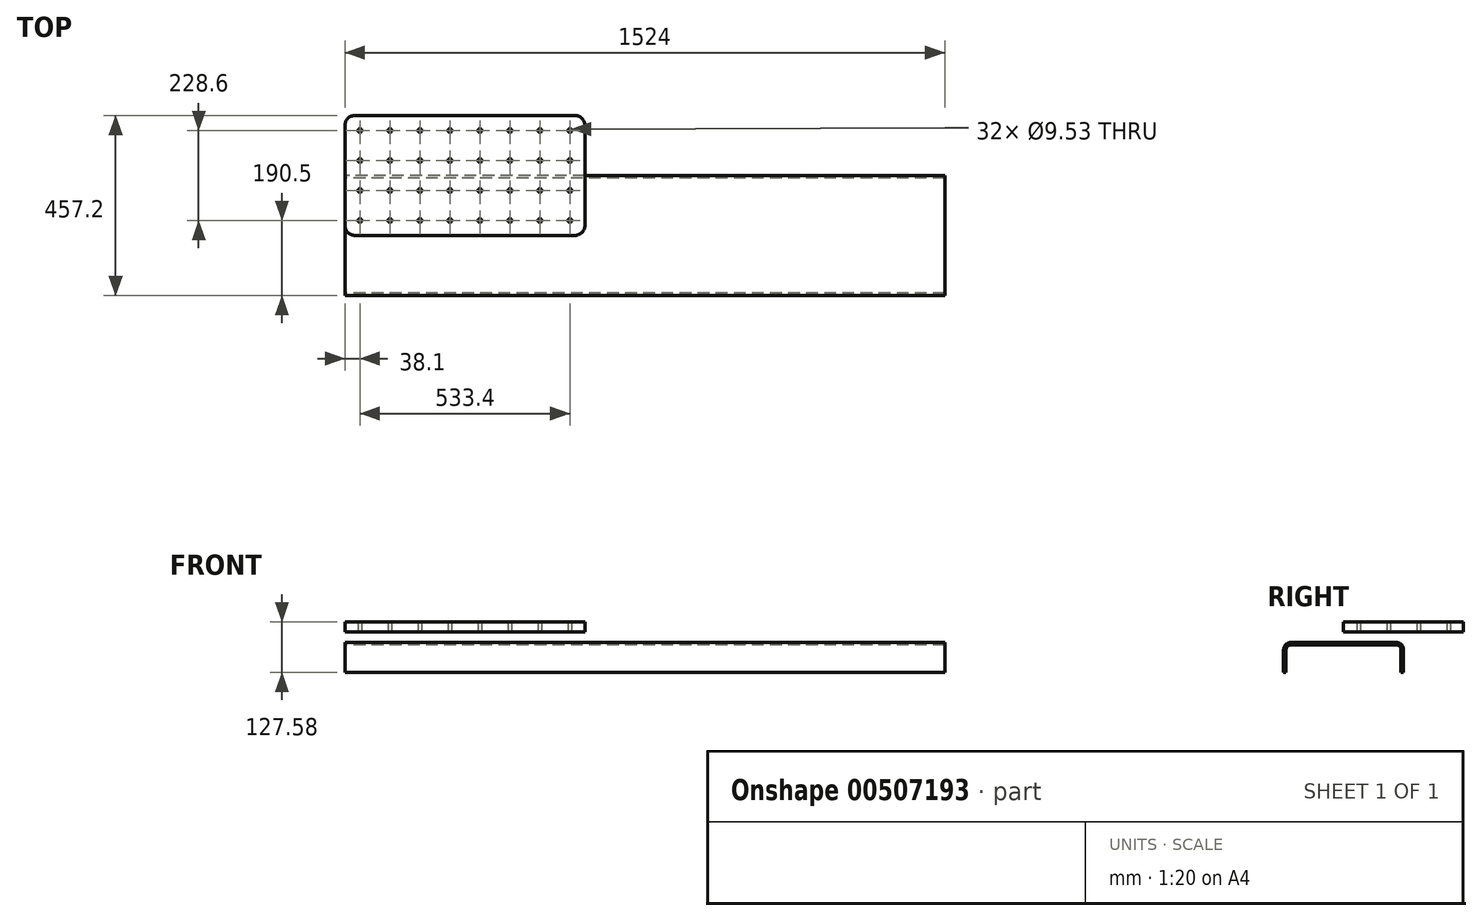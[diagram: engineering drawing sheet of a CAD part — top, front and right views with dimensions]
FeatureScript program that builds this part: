
annotation { "Feature Type Name" : "Feature", "Feature Type Description" : "" }
export const myFeature = defineFeature(function(context is Context, id is Id, definition is map)
    precondition{}
    {
        {
            var Q0;
            Q0=qCreatedBy(makeId("Top.planeOp"),FACE);
            var sketch = newSketch(context, id + "F0", { "sketchPlane" : qUnion([Q0])});
            skLineSegment(sketch, "E0", {"start": v(0, 0) * mm, "end": v(0, 304.8) * mm});
            skLineSegment(sketch, "E1", {"start": v(0, 304.8) * mm, "end": v(609.6, 304.8) * mm});
            skLineSegment(sketch, "E2", {"start": v(609.6, 304.8) * mm, "end": v(609.6, 0) * mm});
            skLineSegment(sketch, "E3", {"start": v(609.6, 0) * mm, "end": v(0, 0) * mm});
            skCircle(sketch, "E4", {"center": v(38.1, 38.1) * mm, "radius": 4.76 * mm});
            skCircle(sketch, "E5.0.1.0", {"center": v(38.1, 114.3) * mm, "radius": 4.76 * mm});
            skCircle(sketch, "E5.0.2.0", {"center": v(38.1, 190.5) * mm, "radius": 4.76 * mm});
            skCircle(sketch, "E5.0.3.0", {"center": v(38.1, 266.7) * mm, "radius": 4.76 * mm});
            skCircle(sketch, "E5.1.0.0", {"center": v(114.3, 38.1) * mm, "radius": 4.76 * mm});
            skCircle(sketch, "E5.1.1.0", {"center": v(114.3, 114.3) * mm, "radius": 4.76 * mm});
            skCircle(sketch, "E5.1.2.0", {"center": v(114.3, 190.5) * mm, "radius": 4.76 * mm});
            skCircle(sketch, "E5.1.3.0", {"center": v(114.3, 266.7) * mm, "radius": 4.76 * mm});
            skCircle(sketch, "E5.2.0.0", {"center": v(190.5, 38.1) * mm, "radius": 4.76 * mm});
            skCircle(sketch, "E5.2.1.0", {"center": v(190.5, 114.3) * mm, "radius": 4.76 * mm});
            skCircle(sketch, "E5.2.2.0", {"center": v(190.5, 190.5) * mm, "radius": 4.76 * mm});
            skCircle(sketch, "E5.2.3.0", {"center": v(190.5, 266.7) * mm, "radius": 4.76 * mm});
            skCircle(sketch, "E5.3.0.0", {"center": v(266.7, 38.1) * mm, "radius": 4.76 * mm});
            skCircle(sketch, "E5.3.1.0", {"center": v(266.7, 114.3) * mm, "radius": 4.76 * mm});
            skCircle(sketch, "E5.3.2.0", {"center": v(266.7, 190.5) * mm, "radius": 4.76 * mm});
            skCircle(sketch, "E5.3.3.0", {"center": v(266.7, 266.7) * mm, "radius": 4.76 * mm});
            skCircle(sketch, "E5.4.0.0", {"center": v(342.9, 38.1) * mm, "radius": 4.76 * mm});
            skCircle(sketch, "E5.4.1.0", {"center": v(342.9, 114.3) * mm, "radius": 4.76 * mm});
            skCircle(sketch, "E5.4.2.0", {"center": v(342.9, 190.5) * mm, "radius": 4.76 * mm});
            skCircle(sketch, "E5.4.3.0", {"center": v(342.9, 266.7) * mm, "radius": 4.76 * mm});
            skCircle(sketch, "E5.5.0.0", {"center": v(419.1, 38.1) * mm, "radius": 4.76 * mm});
            skCircle(sketch, "E5.5.1.0", {"center": v(419.1, 114.3) * mm, "radius": 4.76 * mm});
            skCircle(sketch, "E5.5.2.0", {"center": v(419.1, 190.5) * mm, "radius": 4.76 * mm});
            skCircle(sketch, "E5.5.3.0", {"center": v(419.1, 266.7) * mm, "radius": 4.76 * mm});
            skCircle(sketch, "E5.6.0.0", {"center": v(495.3, 38.1) * mm, "radius": 4.76 * mm});
            skCircle(sketch, "E5.6.1.0", {"center": v(495.3, 114.3) * mm, "radius": 4.76 * mm});
            skCircle(sketch, "E5.6.2.0", {"center": v(495.3, 190.5) * mm, "radius": 4.76 * mm});
            skCircle(sketch, "E5.6.3.0", {"center": v(495.3, 266.7) * mm, "radius": 4.76 * mm});
            skCircle(sketch, "E5.7.0.0", {"center": v(571.5, 38.1) * mm, "radius": 4.76 * mm});
            skCircle(sketch, "E5.7.1.0", {"center": v(571.5, 114.3) * mm, "radius": 4.76 * mm});
            skCircle(sketch, "E5.7.2.0", {"center": v(571.5, 190.5) * mm, "radius": 4.76 * mm});
            skCircle(sketch, "E5.7.3.0", {"center": v(571.5, 266.7) * mm, "radius": 4.76 * mm});
            skLineSegment(sketch, "E5.direction1", {"start": v(38.1, 38.1) * mm, "end": v(114.3, 38.1) * mm, "construction": true});
            skLineSegment(sketch, "E5.direction2", {"start": v(38.1, 38.1) * mm, "end": v(38.1, 114.3) * mm, "construction": true});
            skSolve(sketch);
        }
        {
            var Q0;
            Q0 = qSketchRegion(id + "F0", true);
            extrude(context, id + "F1", {"entities" : qUnion([Q0]), "depth" : 25.4 * mm});
        }
        {
            var Q0;
            Q0=makeQuery(id+"F1.opExtrude","SWEPT_EDGE",EDGE,{"disambiguationData":[OSD([sQuery(id+"F0.wireOp",EDGE,"E0"),sQuery(id+"F0.wireOp",EDGE,"E3")])]});
            var Q1;
            Q1=makeQuery(id+"F1.opExtrude","SWEPT_EDGE",EDGE,{"disambiguationData":[OSD([sQuery(id+"F0.wireOp",EDGE,"E2"),sQuery(id+"F0.wireOp",EDGE,"E3")])]});
            var Q2;
            Q2=makeQuery(id+"F1.opExtrude","SWEPT_EDGE",EDGE,{"disambiguationData":[OSD([sQuery(id+"F0.wireOp",EDGE,"E1"),sQuery(id+"F0.wireOp",EDGE,"E2")])]});
            var Q3;
            Q3=makeQuery(id+"F1.opExtrude","SWEPT_EDGE",EDGE,{"disambiguationData":[OSD([sQuery(id+"F0.wireOp",EDGE,"E0"),sQuery(id+"F0.wireOp",EDGE,"E1")])]});
            fillet(context, id + "F2", {"entities" : qUnion([Q0, Q1, Q2, Q3]), "radius" : 25.4 * mm, "tangentPropagation" : true, "allowEdgeOverflow" : false});
        }
        {
            var Q0;
            Q0=qCreatedBy(makeId("Right.planeOp"),FACE);
            var sketch = newSketch(context, id + "F3", { "sketchPlane" : qUnion([Q0])});
            skLineSegment(sketch, "E6", {"start": v(0, -25.98) * mm, "end": v(-133.35, -25.98) * mm});
            skArc(sketch, "E7", {"start": v(-133.35, -25.98) * mm, "mid": v(-146.82, -31.56) * mm, "end": v(-152.4, -45.03) * mm});
            skLineSegment(sketch, "E8", {"start": v(-152.4, -45.03) * mm, "end": v(-152.4, -102.18) * mm});
            skLineSegment(sketch, "E9", {"start": v(-152.4, -102.18) * mm, "end": v(-146.05, -102.18) * mm});
            skLineSegment(sketch, "E10", {"start": v(-146.05, -102.18) * mm, "end": v(-146.05, -45.03) * mm});
            skArc(sketch, "E11", {"start": v(-146.05, -45.03) * mm, "mid": v(-142.33, -36.05) * mm, "end": v(-133.35, -32.33) * mm});
            skLineSegment(sketch, "E12", {"start": v(-133.35, -32.33) * mm, "end": v(0, -32.33) * mm});
            skLineSegment(sketch, "E13.MirrorCS", {"start": v(152.4, -102.18) * mm, "end": v(146.05, -102.18) * mm});
            skLineSegment(sketch, "E14.MirrorCS", {"start": v(0, -25.98) * mm, "end": v(133.35, -25.98) * mm});
            skArc(sketch, "E15.MirrorCS", {"start": v(133.35, -25.98) * mm, "mid": v(146.82, -31.56) * mm, "end": v(152.4, -45.03) * mm});
            skLineSegment(sketch, "E16.MirrorCS", {"start": v(133.35, -32.33) * mm, "end": v(0, -32.33) * mm});
            skLineSegment(sketch, "E17.MirrorCS", {"start": v(146.05, -102.18) * mm, "end": v(146.05, -45.03) * mm});
            skLineSegment(sketch, "E18.MirrorCS", {"start": v(152.4, -45.03) * mm, "end": v(152.4, -102.18) * mm});
            skArc(sketch, "E19.MirrorCS", {"start": v(146.05, -45.03) * mm, "mid": v(142.33, -36.05) * mm, "end": v(133.35, -32.33) * mm});
            skSolve(sketch);
        }
        {
            var Q0;
            Q0 = qSketchRegion(id + "F3", true);
            extrude(context, id + "F4", {"entities" : qUnion([Q0]), "depth" : 1524 * mm});
        }
    });
